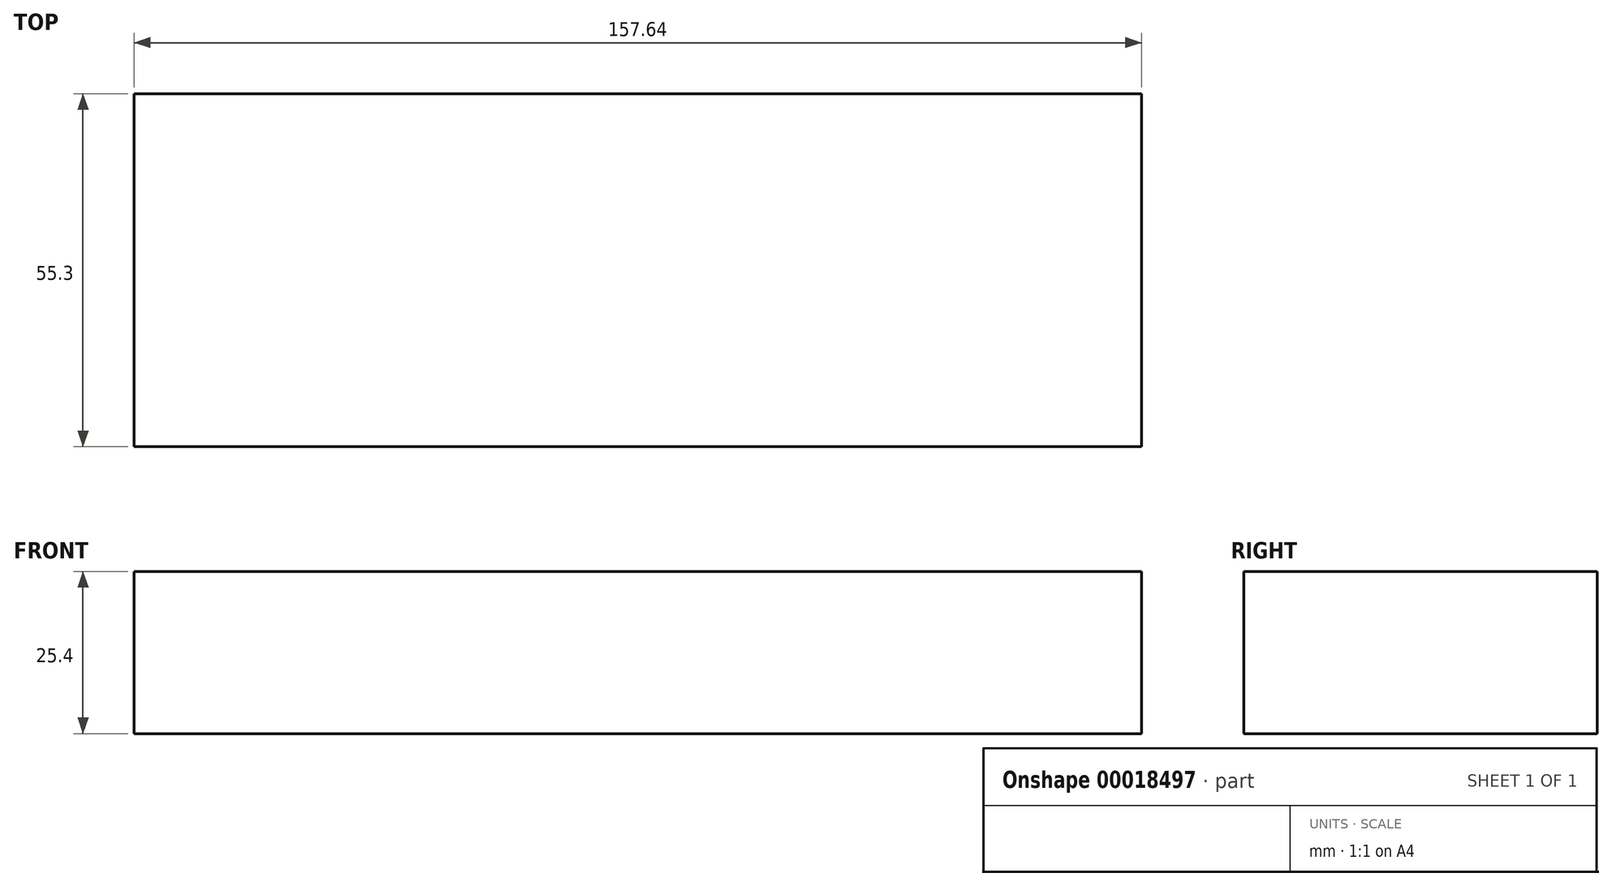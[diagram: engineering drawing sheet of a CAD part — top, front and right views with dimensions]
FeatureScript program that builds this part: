
annotation { "Feature Type Name" : "Feature", "Feature Type Description" : "" }
export const myFeature = defineFeature(function(context is Context, id is Id, definition is map)
    precondition{}
    {
        {
            var Q0;
            Q0=qCreatedBy(makeId("Top.planeOp"),FACE);
            var sketch = newSketch(context, id + "F0", { "sketchPlane" : qUnion([Q0])});
            skLineSegment(sketch, "E0.rect.bottom", {"start": v(-78.82, 27.65) * mm, "end": v(78.82, 27.65) * mm});
            skLineSegment(sketch, "E0.rect.top", {"start": v(-78.82, -27.65) * mm, "end": v(78.82, -27.65) * mm});
            skLineSegment(sketch, "E0.rect.left", {"start": v(-78.82, 27.65) * mm, "end": v(-78.82, -27.65) * mm});
            skLineSegment(sketch, "E0.rect.right", {"start": v(78.82, 27.65) * mm, "end": v(78.82, -27.65) * mm});
            skPoint(sketch, "E0.rect.middle", {"position": v(0, 0) * mm});
            skSolve(sketch);
        }
        {
            var Q0;
            Q0=makeQuery(id+"F0.imprint","IMPRINT",FACE,{"disambiguationData":[TD([[makeQuery(id+"F0.imprint","IMPRINT",EDGE,{"derivedFrom":sQuery(id+"F0.wireOp",EDGE,"E0.rect.bottom")}),-1.0]])]});
            extrude(context, id + "F1", {"entities" : qUnion([Q0]), "depth" : 25.4 * mm});
        }
    });
